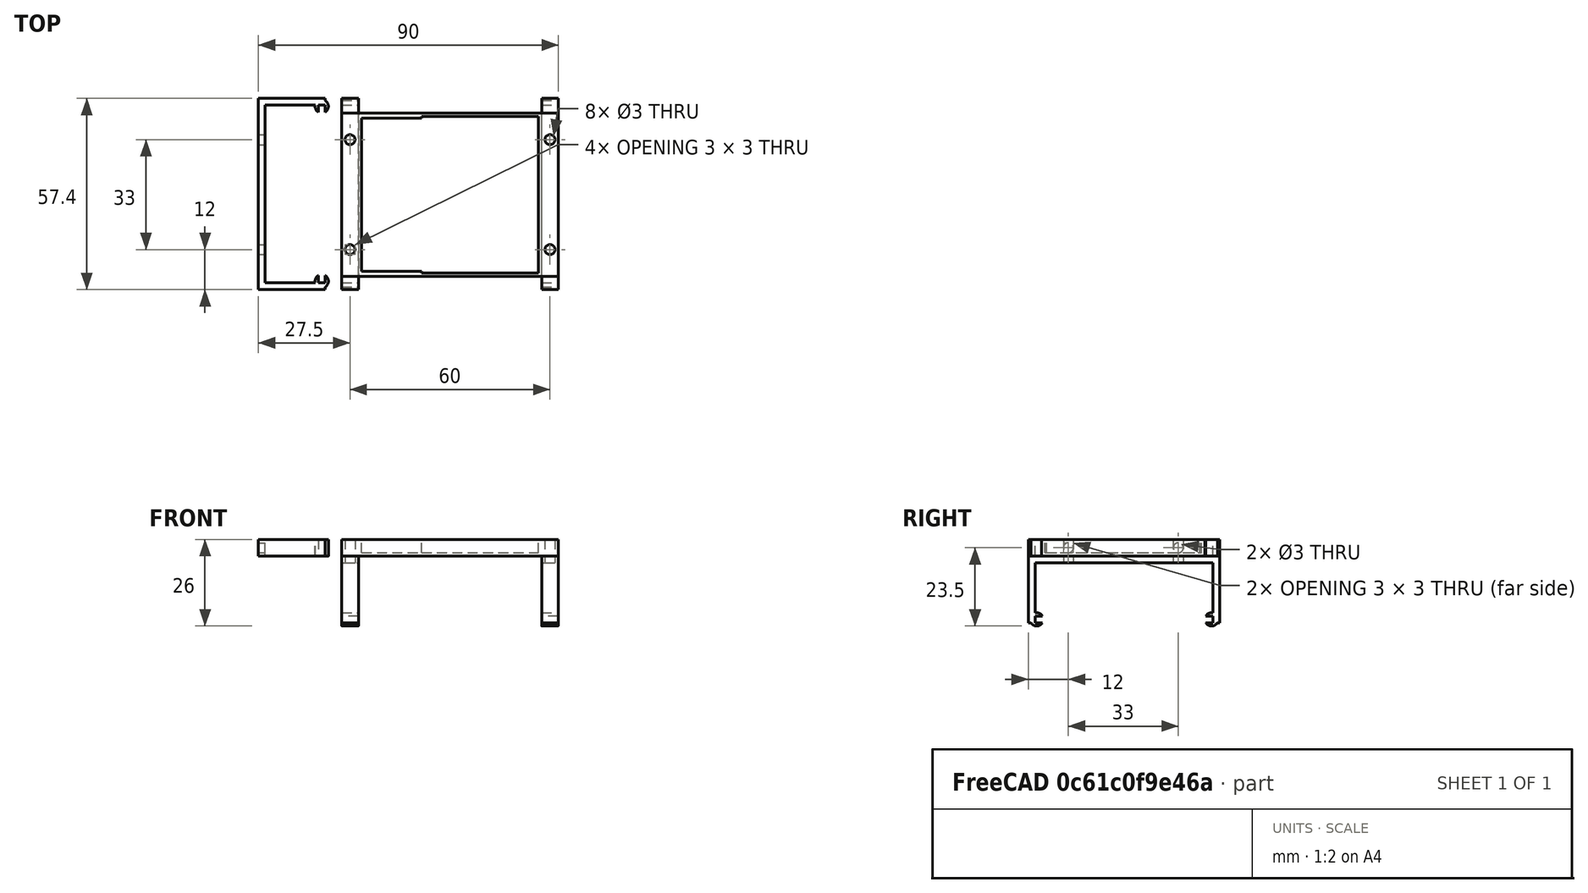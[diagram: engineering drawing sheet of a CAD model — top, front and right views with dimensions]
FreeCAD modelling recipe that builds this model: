
FCSTD DOCUMENT  (FreeCAD 0.14R3702 (Git))
Label: Estructuraparaleskybot
License: CC-BY 3.0
LicenseURL: http://creativecommons.org/licenses/by/3.0/
objects: Part::Cut×7, Part::Box×5, Part::MultiFuse×5, Part::Feature×3, Part::Cylinder×2
note: 22 computed .brp shape members not serialized (recipe doc carries the construction recipe); baked Part::Feature solids carry a one-line shape summary decoded from their .brp

FEATURE [Part::Feature] Part__Feature  label="Arduino"
  Placement = pos=(0,0,0) rot=(1,0,0;1.5708rad)
  shape: bbox 68.58 x 53.34 x 2 mm, 672 faces (baked)
FEATURE [Part::Box] Box  label="Cubo"
  Height = 20
  Length = 5
  Placement = pos=(0,-2,0) rot=(0,0,1;0rad)
  Width = 57.403
FEATURE [Part::Box] Box001  label="Cubo001"
  Height = 20
  Length = 7
  Placement = pos=(0,0,-2) rot=(0,0,1;0rad)
  Width = 53.403
FEATURE [Part::Cut] Cut
  Base = -> Box
  Tool = -> Box001
FEATURE [Part::Cylinder] Cylinder  label="Cilindro"
  Angle = 360
  Height = 5
  Placement = pos=(0,0.5,1) rot=(0.57735,0.57735,0.57735;2.0944rad)
  Radius = 2
FEATURE [Part::Cylinder] Cylinder001  label="Cilindro001"
  Angle = 360
  Height = 5
  Placement = pos=(0,53,1) rot=(0.57735,0.57735,0.57735;2.0944rad)
  Radius = 2
FEATURE [Part::MultiFuse] Fusion
  Shapes = -> [Cylinder,Cylinder001,Cut]
FEATURE [Part::Cut] Cut001
  Base = -> Fusion
  Tool = -> Part__Feature
FEATURE [Part::Feature] Part__Feature001  label="Chamfer001"
  Placement = pos=(2.5,10,25) rot=(0,0,1;0rad)
  shape: bbox 5.5 x 5.5 x 13 mm, 16 faces (baked)
FEATURE [Part::Feature] Part__Feature002  label="Chamfer002"
  Placement = pos=(2.5,43,25) rot=(0,0,1;0rad)
  shape: bbox 5.5 x 5.5 x 13 mm, 16 faces (baked)
FEATURE [Part::MultiFuse] Fusion001
  Shapes = -> [Part__Feature001,Part__Feature002]
FEATURE [Part::Cut] Cut002  label="PatasTraseras"
  Base = -> Cut001
  Tool = -> Fusion001
FEATURE [Part::Box] Box002  label="Cubo002"
  Height = 5
  Length = 65
  Placement = pos=(0,2,20) rot=(0,0,1;0rad)
  Width = 49
FEATURE [Part::MultiFuse] Fusion002
  Placement = pos=(60,0,0) rot=(0,0,1;0rad)
  Shapes = -> [Part__Feature001,Part__Feature002]
FEATURE [Part::Cut] Cut003  label="PatasDelanteras"
  Base = -> Cut001
  Placement = pos=(60,0,0) rot=(0,0,1;0rad)
  Tool = -> Fusion001
FEATURE [Part::MultiFuse] Fusion003  label="Tornillos"
  Shapes = -> [Fusion001,Fusion002]
FEATURE [Part::Box] Box003  label="Cubo003"
  Height = 27
  Length = 18
  Placement = pos=(6,3.5,21) rot=(0,0,1;0rad)
  Width = 46
FEATURE [Part::Box] Box004  label="Cubo004"
  Height = 10
  Length = 35
  Placement = pos=(24,3,21) rot=(0,0,1;0rad)
  Width = 47
FEATURE [Part::Cut] Cut004
  Base = -> Box002
  Tool = -> Fusion003
FEATURE [Part::MultiFuse] Fusion004  label="PilaYproto"
  Shapes = -> [Box003,Box004]
FEATURE [Part::Cut] Cut005  label="Plataforma"
  Base = -> Cut004
  Tool = -> Fusion004
FEATURE [Part::Cut] Cut006  label="Patas Giradas"
  Base = -> Cut001
  Placement = pos=(-5,0,20) rot=(0,-1,0;1.5708rad)
  Tool = -> Fusion001
